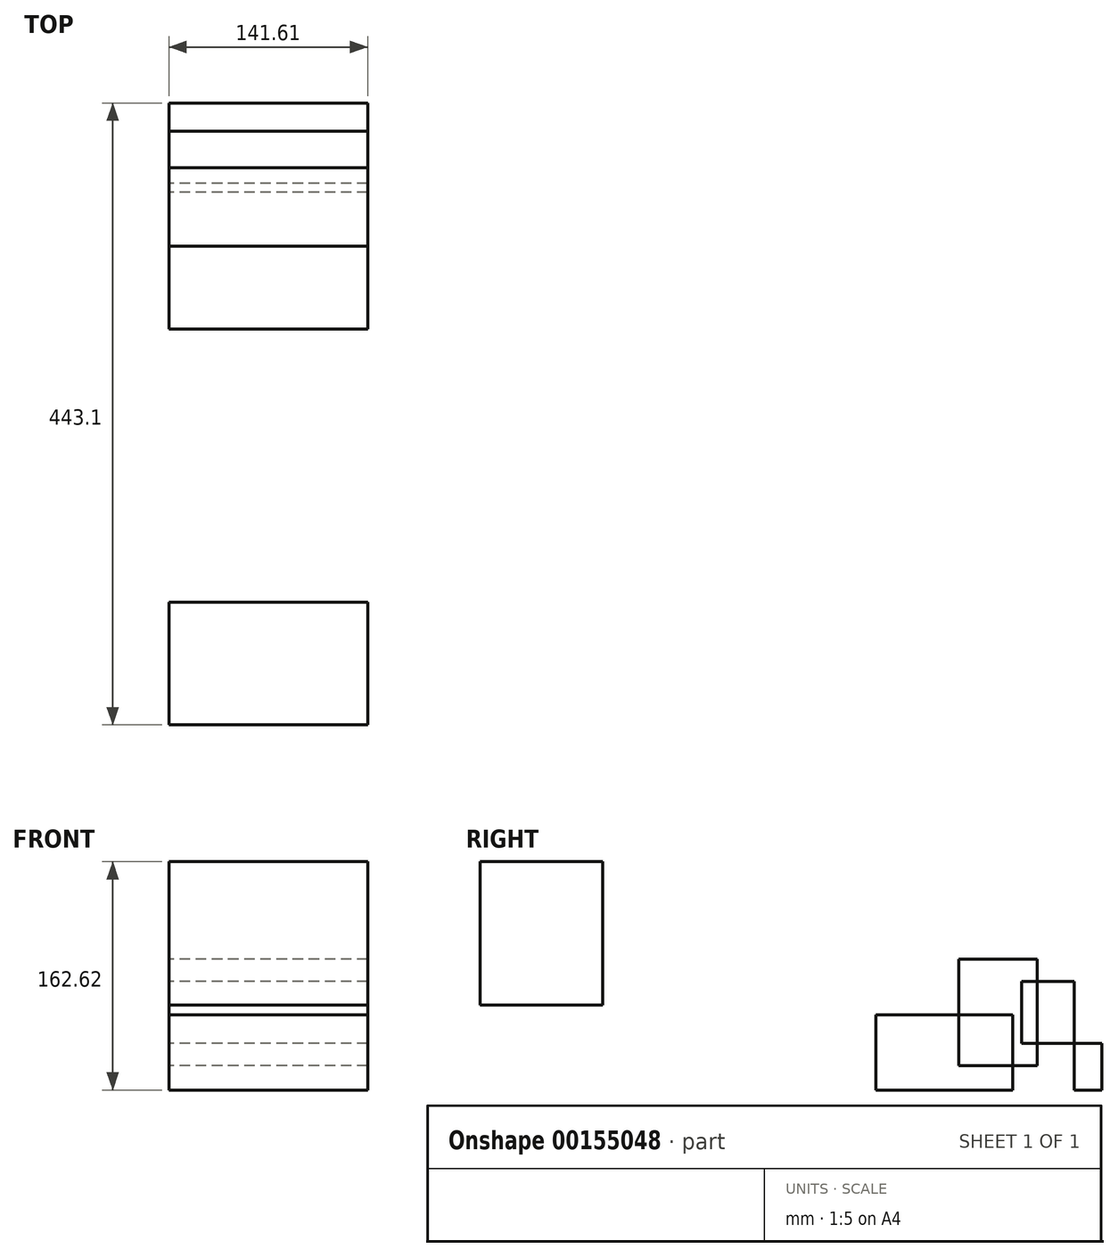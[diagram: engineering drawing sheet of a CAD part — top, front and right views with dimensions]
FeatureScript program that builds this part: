
annotation { "Feature Type Name" : "Feature", "Feature Type Description" : "" }
export const myFeature = defineFeature(function(context is Context, id is Id, definition is map)
    precondition{}
    {
        {
            var Q0;
            Q0=qCreatedBy(makeId("Right.planeOp"),FACE);
            var sketch = newSketch(context, id + "F0", { "sketchPlane" : qUnion([Q0])});
            skLineSegment(sketch, "E0.bottom", {"start": v(143.66, -18.36) * mm, "end": v(88.01, -18.36) * mm});
            skLineSegment(sketch, "E0.top", {"start": v(143.66, -94) * mm, "end": v(88.01, -94) * mm});
            skLineSegment(sketch, "E0.left", {"start": v(143.66, -18.36) * mm, "end": v(143.66, -94) * mm});
            skLineSegment(sketch, "E0.right", {"start": v(88.01, -18.36) * mm, "end": v(88.01, -94) * mm});
            skLineSegment(sketch, "E1.bottom", {"start": v(126.25, -57.87) * mm, "end": v(28.8, -57.87) * mm});
            skLineSegment(sketch, "E1.top", {"start": v(126.25, -111.46) * mm, "end": v(28.8, -111.46) * mm});
            skLineSegment(sketch, "E1.left", {"start": v(126.25, -57.87) * mm, "end": v(126.25, -111.46) * mm});
            skLineSegment(sketch, "E1.right", {"start": v(28.8, -57.87) * mm, "end": v(28.8, -111.46) * mm});
            skLineSegment(sketch, "E2.bottom", {"start": v(132.83, -34) * mm, "end": v(189.93, -34) * mm});
            skLineSegment(sketch, "E2.top", {"start": v(132.83, -78.3) * mm, "end": v(189.93, -78.3) * mm});
            skLineSegment(sketch, "E2.left", {"start": v(132.83, -34) * mm, "end": v(132.83, -78.3) * mm});
            skLineSegment(sketch, "E2.right", {"start": v(189.93, -34) * mm, "end": v(189.93, -78.3) * mm});
            skLineSegment(sketch, "E3.bottom", {"start": v(189.93, -34) * mm, "end": v(170, -34) * mm});
            skLineSegment(sketch, "E3.top", {"start": v(189.93, -111.46) * mm, "end": v(170, -111.46) * mm});
            skLineSegment(sketch, "E3.left", {"start": v(189.93, -34) * mm, "end": v(189.93, -111.46) * mm});
            skLineSegment(sketch, "E3.right", {"start": v(170, -34) * mm, "end": v(170, -111.46) * mm});
            skLineSegment(sketch, "E4.bottom", {"start": v(-253.17, -51.02) * mm, "end": v(-165.69, -51.02) * mm});
            skLineSegment(sketch, "E4.top", {"start": v(-253.17, 51.16) * mm, "end": v(-165.69, 51.16) * mm});
            skLineSegment(sketch, "E4.left", {"start": v(-253.17, -51.02) * mm, "end": v(-253.17, 51.16) * mm});
            skLineSegment(sketch, "E4.right", {"start": v(-165.69, -51.02) * mm, "end": v(-165.69, 51.16) * mm});
            skLineSegment(sketch, "E5", {"start": v(-226.8, -133.88) * mm, "end": v(-327.33, -390.46) * mm});
            skLineSegment(sketch, "E6", {"start": v(-257.68, -212.68) * mm, "end": v(-317.68, -212.68) * mm});
            skLineSegment(sketch, "E7", {"start": v(-317.68, -212.68) * mm, "end": v(-327.33, -390.46) * mm});
            skLineSegment(sketch, "E8", {"start": v(-232.97, -221) * mm, "end": v(-232.97, -100.81) * mm});
            skLineSegment(sketch, "E9", {"start": v(-232.97, -100.81) * mm, "end": v(-317.68, -212.68) * mm});
            skLineSegment(sketch, "E10", {"start": v(-327.33, -390.46) * mm, "end": v(-232.97, -221) * mm});
            skLineSegment(sketch, "E11", {"start": v(-257.68, -212.68) * mm, "end": v(-232.97, -221) * mm});
            skCircle(sketch, "E12", {"center": v(-327.33, -439.27) * mm, "radius": 34.94 * mm});
            skSolve(sketch);
        }
        {
            var Q0;
            {var subQ0=sQuery(id+"F0.wireOp",EDGE,"E1.top");Q0=makeQuery(id+"F0.imprint","IMPRINT",FACE,{"disambiguationData":[TD([[makeQuery(id+"F0.imprint","IMPRINT",EDGE,{"derivedFrom":subQ0}),-1.0]])]});}
            var Q1;
            {var subQ5=sQuery(id+"F0.wireOp",EDGE,"E3.bottom");Q1=makeQuery(id+"F0.imprint","IMPRINT",FACE,{"disambiguationData":[TD([[makeQuery(id+"F0.imprint","IMPRINT",EDGE,{"derivedFrom":subQ5}),1.0]])]});}
            var Q2;
            {var subQ5=sQuery(id+"F0.wireOp",EDGE,"E3.top");Q2=makeQuery(id+"F0.imprint","IMPRINT",FACE,{"disambiguationData":[TD([[makeQuery(id+"F0.imprint","IMPRINT",EDGE,{"derivedFrom":subQ5}),-1.0]])]});}
            var Q3;
            {var subQ6=sQuery(id+"F0.wireOp",EDGE,"E0.bottom");Q3=makeQuery(id+"F0.imprint","IMPRINT",FACE,{"disambiguationData":[TD([[makeQuery(id+"F0.imprint","IMPRINT",EDGE,{"derivedFrom":subQ6}),1.0]])]});}
            var Q4;
            {var subQ0=sQuery(id+"F0.wireOp",EDGE,"E2.bottom");var subQ1=sQuery(id+"F0.wireOp",EDGE,"E0.left");var subQ2=makeQuery(id+"F0.imprint","INTERSECT",VERTEX,{"derivedFrom":[subQ1,subQ0]});Q4=makeQuery(id+"F0.imprint","IMPRINT",FACE,{"disambiguationData":[TD([[makeQuery(id+"F0.imprint","IMPRINT",EDGE,{"disambiguationData":[TD([[subQ2,-1.0]])],"derivedFrom":subQ1}),1.0]])]});}
            var Q5;
            Q5=makeQuery(id+"F0.imprint","IMPRINT",FACE,{"disambiguationData":[TD([[makeQuery(id+"F0.imprint","IMPRINT",EDGE,{"derivedFrom":sQuery(id+"F0.wireOp",EDGE,"E4.bottom")}),1.0]])]});
            extrude(context, id + "F1", {"entities" : qUnion([Q0, Q1, Q2, Q3, Q4, Q5]), "depth" : 141.6 * mm});
        }
    });
